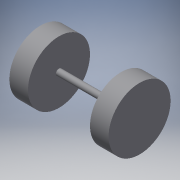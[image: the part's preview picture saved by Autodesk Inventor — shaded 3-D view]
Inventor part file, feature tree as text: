
AUTODESK INVENTOR PART (.ipt)
format: ipt  version: 2019 (Build 230136000, 136)  size: 109,568 bytes
history: native  units: in
note: dims shown in document units (in); Inventor stores cm internally (conversion verified against a paired STEP export)
features: extrude x3, sketch x3
ambient origin geometry x8: Origin, YZ Plane, XZ Plane, XY Plane, X Axis, Y Axis, Z Axis, Center Point
bodies: Solid1 (feature_tree)
feature tree (6):
  extrude  "Extrusion1"  Depth=5.0in TaperAngle=0.0deg
  extrude  "Extrusion2"  Depth=1.5in TaperAngle=0.0deg
  extrude  "Extrusion3"  Depth=1.5in TaperAngle=0.0deg
  sketch  "Sketch1"  dims[d0=0.5in d1=5.0in d2=0.0in]
  sketch  "Sketch2"  dims[d3=5.0in d4=1.5in d5=0.0in]
  sketch  "Sketch3"  dims[d6=5.0in d7=1.5in d8=0.0in]
